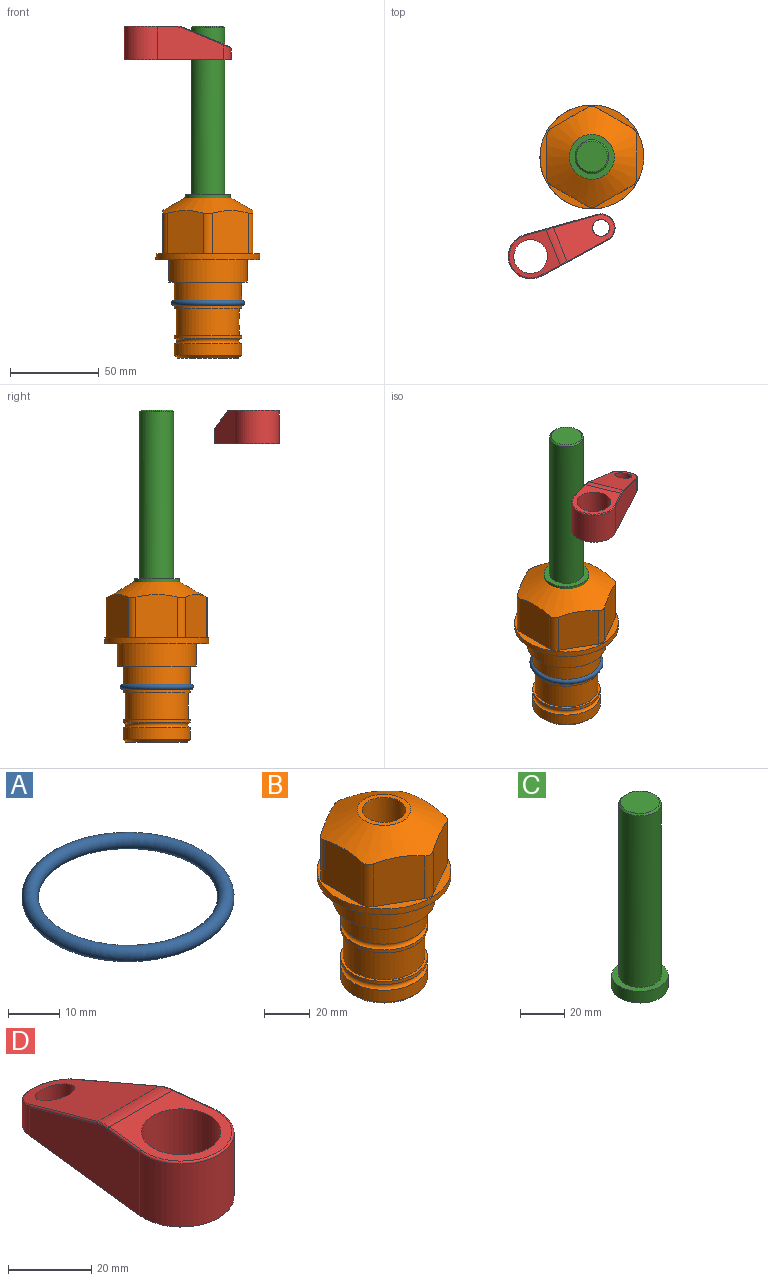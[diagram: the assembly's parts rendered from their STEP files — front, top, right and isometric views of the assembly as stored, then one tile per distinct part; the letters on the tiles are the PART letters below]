
ASSEMBLY  parts=4 mates=2
PART A: 1 faces, bbox 44.7x44.7x3.2 mm
  f0: torus R=19.05mm, axis (0,0,1), area 1193.9mm2
PART B: 36 faces, bbox 58.7x58.7x91.2 mm
  f0: cylinder r=17.78mm len=35.56mm, axis (0,0,1), area 1670.8mm2, adj f23,f24,f31
  f1: cylinder r=19.05mm len=38.1mm, axis (0,0,1), area 1191.9mm2, adj f26,f27,f30
  f2: plane 58.66x58.66mm, normal (0,0,-1), area 1150.6mm2, adj f3,f28
  f3: cylinder r=29.33mm len=58.66mm, axis (0,0,-1), area 585.1mm2, adj f2,f4
  f4: plane 58.66x58.66mm, normal (0,0,1), area 475.9mm2, adj f3,f5,f6,f7,f8,f9,f10,f11
  f5: plane 24.5x20.32mm, normal (-0.5,0.87,0), area 562.8mm2, adj f4,f15,f16,f17
  f6: plane 24.5x20.32mm, normal (0.5,0.87,0), area 562.8mm2, adj f4,f14,f15,f17
  f7: plane 24.5x23.48mm, normal (1,0,0), area 562.8mm2, adj f4,f13,f14,f17
  f8: plane 24.5x20.32mm, normal (0.5,-0.87,0), area 562.8mm2, adj f4,f12,f13,f17
  f9: plane 24.5x20.32mm, normal (-0.5,-0.87,0), area 562.8mm2, adj f4,f11,f12,f17
  f10: plane 24.5x23.48mm, normal (-1,0,0), area 562.8mm2, adj f4,f11,f16,f17
  f11: cylinder r=5.08mm len=23.01mm, axis (0,0,-1), area 121.2mm2, adj f4,f9,f10,f17
  f12: cylinder r=5.08mm len=23.01mm, axis (0,0,-1), area 121.2mm2, adj f4,f8,f9,f17
  f13: cylinder r=5.08mm len=23.01mm, axis (0,0,-1), area 121.2mm2, adj f4,f7,f8,f17
  f14: cylinder r=5.08mm len=23.01mm, axis (0,0,-1), area 121.2mm2, adj f4,f6,f7,f17
  f15: cylinder r=5.08mm len=23.01mm, axis (0,0,-1), area 121.2mm2, adj f4,f5,f6,f17
  f16: cylinder r=5.08mm len=23.01mm, axis (0,0,-1), area 121.2mm2, adj f4,f5,f10,f17
  f17: cone r=11.73mm half-angle=60deg, axis (0,0,-1), area 2071.8mm2, adj f5,f6,f7,f8,f9,f10,f11,f12
  f18: plane 23.46x23.46mm, normal (0,0,1), area 147.4mm2, adj f17,f35
  f19: plane 34.93x34.93mm, normal (0,0,-1), area 958mm2, adj f29
  f20: cylinder r=19.05mm len=38.1mm, axis (0,0,1), area 760.1mm2, adj f21,f29
  f21: torus R=19.05mm, axis (0,0,1), area 565.3mm2, adj f20,f22
  f22: cylinder r=19.05mm len=38.1mm, axis (0,0,1), area 190mm2, adj f21,f23
  f23: plane 38.1x38.1mm, normal (0,0,1), area 146.9mm2, adj f0,f22
  f24: plane 38.1x38.1mm, normal (0,0,-1), area 146.9mm2, adj f0,f25
  f25: cylinder r=19.05mm len=38.1mm, axis (0,0,1), area 190mm2, adj f24,f26
  f26: torus R=19.05mm, axis (0,0,1), area 565.3mm2, adj f1,f25
  f27: plane 44.45x44.45mm, normal (0,0,-1), area 411.7mm2, adj f1,f28
  f28: cylinder r=22.23mm len=44.45mm, axis (0,0,1), area 1773.5mm2, adj f2,f27
  f29: cone r=19.05mm half-angle=45deg, axis (0,0,1), area 257.5mm2, adj f19,f20
  f30: cylinder r=3.17mm len=6.75mm, axis (-1,0,0), area 128mm2, adj f1,f33
  f31: cylinder r=3.17mm len=6.35mm, axis (-1,0,0), area 102.5mm2, adj f0,f33
  f32: plane 25.4x25.4mm, normal (0,0,1), area 506.7mm2, adj f33
  f33: cylinder r=12.7mm len=66.42mm, axis (0,0,-1), area 5236.2mm2, adj f30,f31,f32,f34
  f34: cone r=9.53mm half-angle=30deg, axis (0,0,-1), area 443.4mm2, adj f33,f35
  f35: cylinder r=9.53mm len=19.05mm, axis (0,0,-1), area 849mm2, adj f18,f34
PART C: 6 faces, bbox 25.4x25.4x101.6 mm
  f0: plane 17.46x17.46mm, normal (0,0,1), area 239.5mm2, adj f5
  f1: plane 25.4x25.4mm, normal (0,0,-1), area 506.7mm2, adj f2
  f2: cylinder r=12.7mm len=25.4mm, axis (0,0,1), area 506.7mm2, adj f1,f3
  f3: plane 25.4x25.4mm, normal (0,0,1), area 221.7mm2, adj f2,f4
  f4: cylinder r=9.53mm len=94.46mm, axis (0,0,1), area 5653mm2, adj f3,f5
  f5: cone r=8.73mm half-angle=45deg, axis (0,0,-1), area 64.4mm2, adj f0,f4
PART D: 44 faces, bbox 27.5x64.5x19.1 mm
  f0: plane 2.3x0.95mm, normal (0,0,-1), area 1mm2, adj f25,f30,f34
  f1: plane 63.5x25.4mm, normal (0,0,-1), area 561.7mm2, adj f2,f3,f4,f5,f6,f7,f19,f20
  f2: cylinder r=12.7mm len=25.4mm, axis (0,0,-1), area 792.2mm2, adj f1,f3,f5,f13
  f3: plane 42.33x18.54mm, normal (0.99,0.11,0), area 647mm2, adj f1,f2,f4,f11,f12,f14
  f4: cylinder r=7.94mm len=15.78mm, axis (0,0,-1), area 158.6mm2, adj f1,f3,f5,f16
  f5: plane 42.33x18.54mm, normal (-0.99,0.11,0), area 647mm2, adj f1,f2,f4,f15,f17,f18
  f6: cylinder r=9.53mm len=19.05mm, axis (0,0,-1), area 1140.1mm2, adj f1,f8
  f7: cylinder r=4.76mm len=10.98mm, axis (0,0,-1), area 276.1mm2, adj f1,f9
  f8: plane 25.83x24.38mm, normal (0,0,1), area 262.2mm2, adj f6,f10,f11,f13,f15
  f9: plane 32.49x20.55mm, normal (0,0.34,0.94), area 489.9mm2, adj f7,f10,f14,f16,f18
  f10: cylinder r=12.7mm len=21.49mm, axis (-1,0,0), area 93.2mm2, adj f8,f9,f12,f17
  f11: cylinder r=0.51mm len=12.34mm, axis (0.11,-0.99,0), area 9.9mm2, adj f3,f8,f12,f13
  f12: bspline ~7.62x1.64mm, area 3.5mm2, adj f3,f10,f11,f14
  f13: torus R=12.19mm, axis (0,0,1), area 33.6mm2, adj f2,f8,f11,f15
  f14: cylinder r=0.51mm len=26.01mm, axis (0.1,-0.93,0.34), area 21.6mm2, adj f3,f9,f12,f16
  f15: cylinder r=0.51mm len=12.34mm, axis (0.11,0.99,0), area 9.9mm2, adj f5,f8,f13,f17
  f16: bspline ~15.78x7.05mm, area 15.7mm2, adj f4,f9,f14,f18
  f17: bspline ~7.62x1.64mm, area 3.5mm2, adj f5,f10,f15,f18
  f18: cylinder r=0.51mm len=26.01mm, axis (0.1,0.93,-0.34), area 21.6mm2, adj f5,f9,f16,f17
  f19: plane 21.6x14.29mm, normal (-0.99,-0.11,0), area 242.6mm2, adj f1,f26,f28,f34,f36,f38
  f20: plane 21.6x14.29mm, normal (0.99,-0.11,0), area 242.6mm2, adj f1,f27,f29,f37,f39,f41
  f21: cylinder r=12.7mm len=14.29mm, axis (0,0,-1), area 173.2mm2, adj f1,f26,f27,f30,f31,f33
  f22: cylinder r=7.94mm len=7.63mm, axis (0,0,-1), area 53.8mm2, adj f1,f28,f29,f42
  f23: plane 2.3x0.95mm, normal (0,0,-1), area 1mm2, adj f25,f33,f37
  f24: plane 17.94x12.32mm, normal (0,-0.34,-0.94), area 191.2mm2, adj f25,f38,f41,f42
  f25: cylinder r=9.53mm len=12.93mm, axis (-1,0,0), area 37.5mm2, adj f0,f23,f24,f31,f36,f39
  f26: cylinder r=1.59mm len=14.29mm, axis (0,0,-1), area 49mm2, adj f1,f19,f21,f32
  f27: cylinder r=1.59mm len=14.29mm, axis (0,0,-1), area 49mm2, adj f1,f20,f21,f35
  f28: cylinder r=1.59mm len=7.28mm, axis (0,0,-1), area 22.1mm2, adj f1,f19,f22,f40
  f29: cylinder r=1.59mm len=7.28mm, axis (0,0,-1), area 22.1mm2, adj f1,f20,f22,f43
  f30: torus R=14.29mm, axis (0,0,1), area 5.8mm2, adj f0,f21,f31,f32
  f31: bspline ~11.06x2.73mm, area 20.8mm2, adj f21,f25,f30,f33
  f32: sphere r=1.59mm, area 5.4mm2, adj f26,f30,f34
  f33: torus R=14.29mm, axis (0,0,1), area 5.8mm2, adj f21,f23,f31,f35
  f34: cylinder r=1.59mm len=1.68mm, axis (-0.11,0.99,0), area 2.4mm2, adj f0,f19,f32,f36
  f35: sphere r=1.59mm, area 5.4mm2, adj f27,f33,f37
  f36: bspline ~5.82x2.33mm, area 7.7mm2, adj f19,f25,f34,f38
  f37: cylinder r=1.59mm len=1.68mm, axis (0.11,0.99,0), area 2.4mm2, adj f20,f23,f35,f39
  f38: cylinder r=1.59mm len=18.33mm, axis (0.1,-0.93,0.34), area 46.7mm2, adj f19,f24,f36,f40
  f39: bspline ~5.82x2.33mm, area 7.7mm2, adj f20,f25,f37,f41
  f40: sphere r=1.59mm, area 3.6mm2, adj f28,f38,f42
  f41: cylinder r=1.59mm len=18.33mm, axis (0.1,0.93,-0.34), area 46.7mm2, adj f20,f24,f39,f43
  f42: bspline ~8.31x1.84mm, area 15.3mm2, adj f22,f24,f40,f43
  f43: sphere r=1.59mm, area 3.6mm2, adj f29,f41,f42
PLACE A at identity
PLACE B at identity fixed
PLACE C rot(axis=(0,0,1),58.5deg) t=(0,0,58.25)mm
PLACE D rot(axis=(0,0,-1),67.9deg) t=(-34.57,-56.44,112.86)mm
MATE pin_slot D.f2 <-> C.f2  axis (0,0,-1) through (-34.57,-56.44,131.91)mm
MATE cylindrical C.f2 <-> B.f0  axis (0,0,1) through (0,0,83.88)mm
